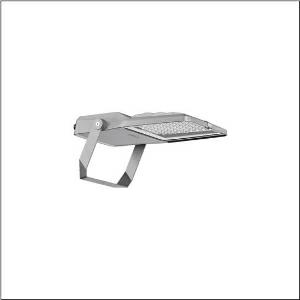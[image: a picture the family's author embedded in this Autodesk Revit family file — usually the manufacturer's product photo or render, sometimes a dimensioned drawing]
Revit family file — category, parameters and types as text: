
# Revit family: floodlight_fl_21_mini___pl64_5xa7771c2e1a_ce65
name_source: partatom
category: Lighting Fixtures
units: mm (PartAtom-declared; Revit-internal decimal feet)

## family parameters
Cut with Voids When Loaded = No
Host = Face
Light Source = No
Part Type = Normal
Room Calculation Point = No
Round Connector Dimension = Use Diameter
Shared = No

## types (1)
- --- (1 x LED, 11790 lm, 87.2 W, 3000K)
    Apparent Load = 87 VA
    CIE Flux Codes = 28 80 98 100 100
    Color Rendering = 70
    Color Temperature = 3000K
    Default Elevation = 1800 mm
    Description = Floodlight FL 21 mini, floodlight, primary light control with lens, of PMMA, primary optical cover: protective disc, of toughened safety glass, transparent, light distribution: PL64, light emission: direct distribution, installation type: surface-mounted, LED, High Power LED, rated luminous flux: 11.790lm, luminous efficacy: 135lm/W, light colour: 730, colour temperature: 3000K, control gear: ECG iQ, control: Auto-Match, Temp-Guard, Lumen-Switch, Night-Set, Smart-Wire, Light-Fading, Desk-Remote (wireless, voltage-free reading and setting of iQ features in the workshop via application-optimized NFC function/RFID function), optimised constant luminous flux control (CLO 2.0), with terminal, 6-pole, mains connection: 220..240V, AC, 50/60Hz, start of lifetime: 87W, end of lifetime: 92W, reduction: 40W, luminaire housing, of diecast aluminium, powder-coated, Siteco® metallic grey (DB 702S), corrosivity category C5 according to DIN EN ISO 12944, mounting bracket, of steel, galvanised, powder-coated, Siteco® metallic grey (DB 702S), protection rating (complete): IP66, insulation class (complete): insulation class II (safety insulation), certification: CE, ENEC, VDE, protection symbol: D, impact resistance: IK08, permissible operating ambient temperature: -40..+40°C, permissible operating ambient temperature for outdoor applications: -40..+50°C, standard: DIN EN 12944, packaging unit: 1 piece

Light Distribution: PL64
    Height = 70 mm
    Lamp = 1 x LED
    Lamp Light Flux = 11790 lm
    Lamp Power = 87.2 W
    Lamp count = 1
    Length = 485 mm
    Luminous efficacy = 135 lm/W
    Manufacturer = Siteco
    ModVariant = No
    Model = 5XA7771C2E1A
    Number of Poles = 1
    OnlyDefault = Yes
    Power Factor = 1
    Product Name = Floodlight FL 21 mini | PL64
    Product group = floodlight | pylon top
    ProductGroupID = 6101
    Protection Class = Protection class II
    Protection Degree = IP 66
    RLX_Detail_Level = 1
    RlxData = <blob elided: 96077 chars, md5=7a75d3ec>
    Socket = socket
    Standby Power = 0 W
    System Light Flux = 11790 lm
    System Power = 87 W
    Type Comments = factory setting: luminous flux: 100 % | dim-lin: 254 | 456 mA
    Type Image = l_1006845.jpg
    URL = http://relux.com
    VarID = @adj_077737
    Voltage = 0 V
    Weight = 0.00 kg
    Width = 337 mm

## geometry (parser evidence)
native form markers: Blend x4, Sweep x11
no freeform markers — native parametric forms only
